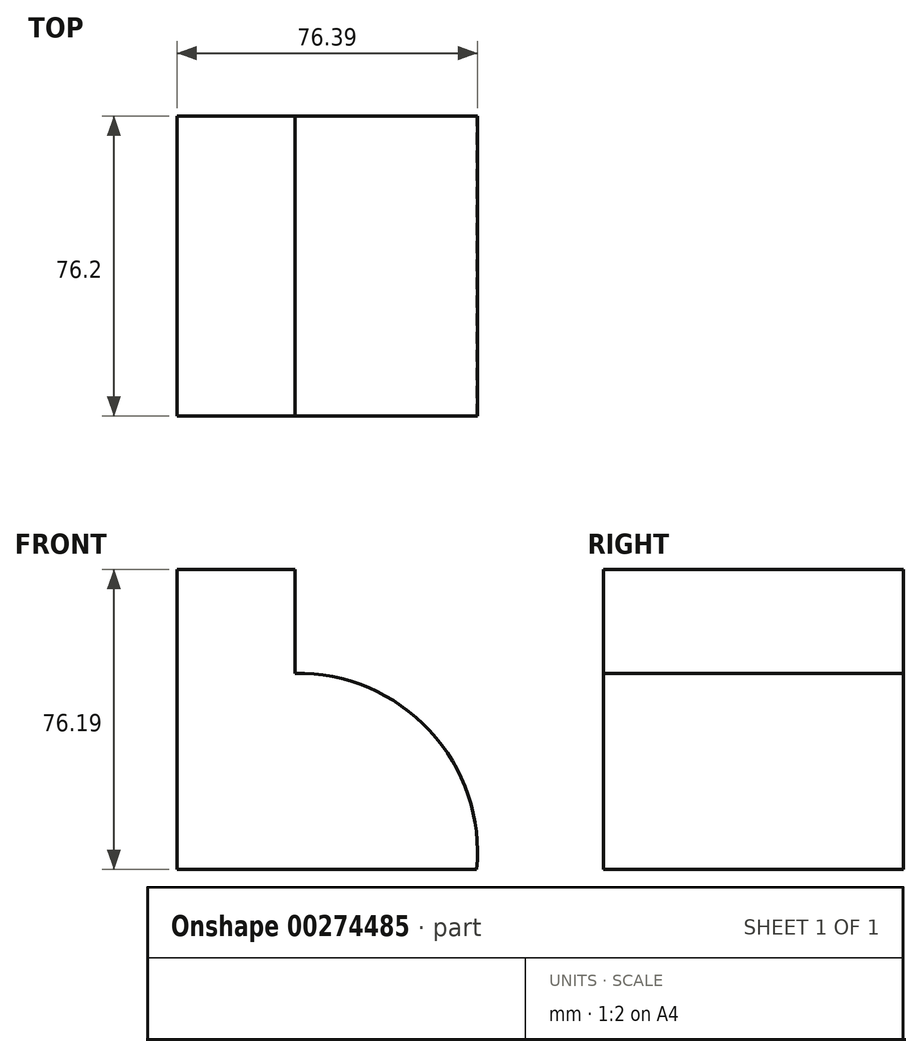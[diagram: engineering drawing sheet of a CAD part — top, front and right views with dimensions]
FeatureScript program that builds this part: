
annotation { "Feature Type Name" : "Feature", "Feature Type Description" : "" }
export const myFeature = defineFeature(function(context is Context, id is Id, definition is map)
    precondition{}
    {
        {
            var Q0;
            Q0=qCreatedBy(makeId("Front.planeOp"),FACE);
            var sketch = newSketch(context, id + "F0", { "sketchPlane" : qUnion([Q0])});
            skLineSegment(sketch, "E0", {"start": v(0, 0) * mm, "end": v(-76.2, 0) * mm});
            skLineSegment(sketch, "E1", {"start": v(-76.2, 0) * mm, "end": v(-76.2, 76.2) * mm});
            skLineSegment(sketch, "E2", {"start": v(-76.2, 76.2) * mm, "end": v(-46.21, 76.2) * mm});
            skLineSegment(sketch, "E3", {"start": v(-46.21, 76.2) * mm, "end": v(-46.21, 49.84) * mm});
            skArc(sketch, "E4", {"start": v(0, 0) * mm, "mid": v(-11.96, 35.26) * mm, "end": v(-46.21, 49.84) * mm});
            skSolve(sketch);
        }
        {
            var Q0;
            Q0=makeQuery(id+"F0.imprint","IMPRINT",FACE,{"disambiguationData":[TD([[makeQuery(id+"F0.imprint","IMPRINT",EDGE,{"derivedFrom":sQuery(id+"F0.wireOp",EDGE,"E0")}),-1.0]])]});
            extrude(context, id + "F1", {"entities" : qUnion([Q0]), "depth" : 76.2 * mm});
        }
    });
